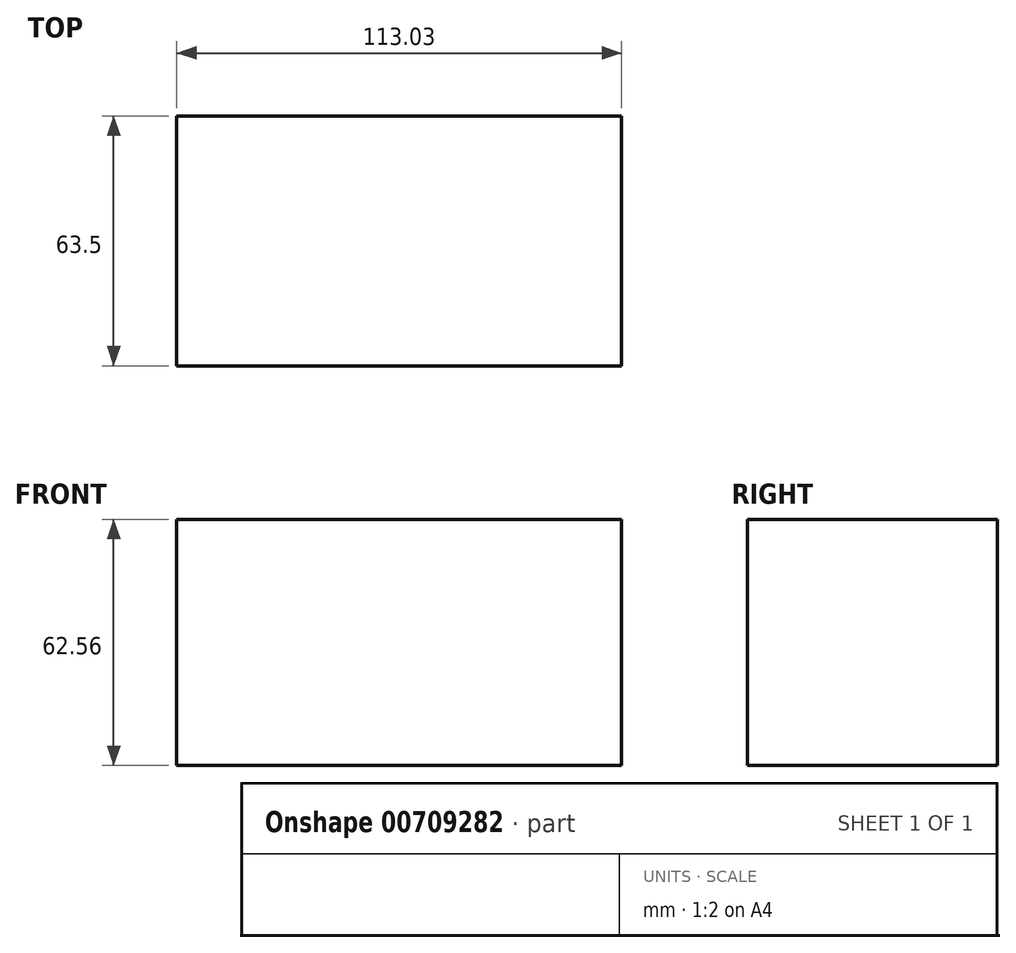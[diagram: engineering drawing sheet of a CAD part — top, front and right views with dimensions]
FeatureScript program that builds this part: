
annotation { "Feature Type Name" : "Feature", "Feature Type Description" : "" }
export const myFeature = defineFeature(function(context is Context, id is Id, definition is map)
    precondition{}
    {
        {
            var Q0;
            Q0=qCreatedBy(makeId("Front.planeOp"),FACE);
            var sketch = newSketch(context, id + "F0", { "sketchPlane" : qUnion([Q0])});
            skLineSegment(sketch, "E0.bottom", {"start": v(-55.7, 32.21) * mm, "end": v(57.33, 32.21) * mm});
            skLineSegment(sketch, "E0.top", {"start": v(-55.7, -30.35) * mm, "end": v(57.33, -30.35) * mm});
            skLineSegment(sketch, "E0.left", {"start": v(-55.7, 32.21) * mm, "end": v(-55.7, -30.35) * mm});
            skLineSegment(sketch, "E0.right", {"start": v(57.33, 32.21) * mm, "end": v(57.33, -30.35) * mm});
            skSolve(sketch);
        }
        {
            var Q0;
            Q0=makeQuery(id+"F0.imprint","IMPRINT",FACE,{"disambiguationData":[TD([[makeQuery(id+"F0.imprint","IMPRINT",EDGE,{"derivedFrom":sQuery(id+"F0.wireOp",EDGE,"E0.bottom")}),-1.0]])]});
            var Q1;
            Q1=sQuery(id+"F0.wireOp",EDGE,"E0.bottom");
            var Q2;
            Q2=sQuery(id+"F0.wireOp",EDGE,"E0.left");
            var Q3;
            Q3=sQuery(id+"F0.wireOp",EDGE,"E0.top");
            var Q4;
            Q4=sQuery(id+"F0.wireOp",EDGE,"E0.right");
            extrude(context, id + "F1", {"entities" : qUnion([Q0]), "surfaceEntities" : qUnion([Q1, Q2, Q3, Q4]), "depth" : 63.5 * mm, "offsetDistance" : 25.4 * mm});
        }
    });
